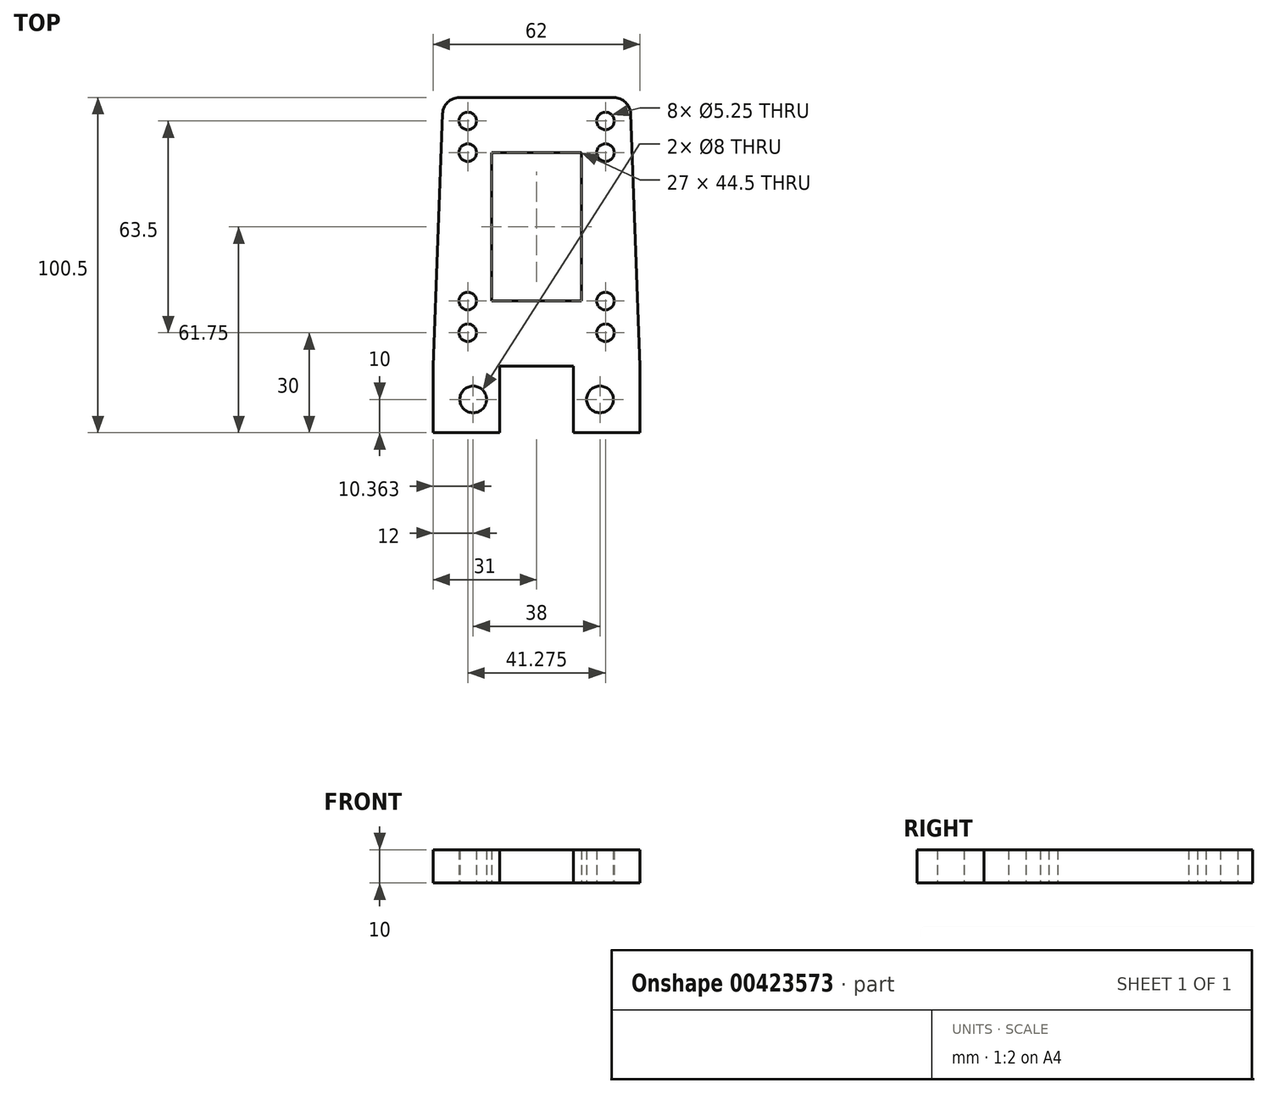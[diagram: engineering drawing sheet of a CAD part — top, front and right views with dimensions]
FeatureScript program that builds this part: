
annotation { "Feature Type Name" : "Feature", "Feature Type Description" : "" }
export const myFeature = defineFeature(function(context is Context, id is Id, definition is map)
    precondition{}
    {
        {
            var Q0;
            Q0=qCreatedBy(makeId("Top.planeOp"),FACE);
            var sketch = newSketch(context, id + "F0", { "sketchPlane" : qUnion([Q0])});
            skLineSegment(sketch, "E0.bottom", {"start": v(28, -50.25) * mm, "end": v(-28, -50.25) * mm});
            skLineSegment(sketch, "E0.top", {"start": v(28, 50.25) * mm, "end": v(-28, 50.25) * mm});
            skLineSegment(sketch, "E0.left", {"start": v(28, -50.25) * mm, "end": v(28, 50.25) * mm});
            skLineSegment(sketch, "E0.right", {"start": v(-28, -50.25) * mm, "end": v(-28, 50.25) * mm});
            skPoint(sketch, "E0.middle", {"position": v(0, 0) * mm});
            skPoint(sketch, "E1", {"position": v(-19, -40.25) * mm});
            skPoint(sketch, "E2", {"position": v(19, -40.25) * mm});
            skLineSegment(sketch, "E3", {"start": v(0, 50.25) * mm, "end": v(0, -50.25) * mm});
            skPoint(sketch, "E4", {"position": v(20.64, -20.25) * mm});
            skPoint(sketch, "E5", {"position": v(-20.64, -20.25) * mm});
            skPoint(sketch, "E6", {"position": v(-20.64, 33.75) * mm});
            skPoint(sketch, "E7", {"position": v(20.64, 33.75) * mm});
            skPoint(sketch, "E8", {"position": v(0, 33.75) * mm});
            skLineSegment(sketch, "E9.bottom", {"start": v(11.05, -50.25) * mm, "end": v(-11.05, -50.25) * mm});
            skLineSegment(sketch, "E9.top", {"start": v(11.05, -30.25) * mm, "end": v(-11.05, -30.25) * mm});
            skLineSegment(sketch, "E9.left", {"start": v(11.05, -50.25) * mm, "end": v(11.05, -30.25) * mm});
            skLineSegment(sketch, "E9.right", {"start": v(-11.05, -50.25) * mm, "end": v(-11.05, -30.25) * mm});
            skPoint(sketch, "E9.middle", {"position": v(0, -40.25) * mm});
            skPoint(sketch, "E10", {"position": v(20.64, 43.25) * mm});
            skPoint(sketch, "E11", {"position": v(-20.64, 43.25) * mm});
            skPoint(sketch, "E12", {"position": v(-20.64, -10.75) * mm});
            skPoint(sketch, "E13", {"position": v(20.64, -10.75) * mm});
            skPoint(sketch, "E14", {"position": v(0, -10.75) * mm});
            skPoint(sketch, "E15", {"position": v(0, 11.5) * mm});
            skLineSegment(sketch, "E16", {"start": v(28, -50.25) * mm, "end": v(31, -50.25) * mm});
            skLineSegment(sketch, "E17", {"start": v(31, -50.25) * mm, "end": v(31, -30.25) * mm});
            skLineSegment(sketch, "E18", {"start": v(31, -30.25) * mm, "end": v(28, 50.25) * mm});
            skLineSegment(sketch, "E19", {"start": v(-28, -50.25) * mm, "end": v(-31, -50.25) * mm});
            skLineSegment(sketch, "E20", {"start": v(-31, -50.25) * mm, "end": v(-31, -30.25) * mm});
            skLineSegment(sketch, "E21", {"start": v(-31, -30.25) * mm, "end": v(-28, 50.25) * mm});
            skLineSegment(sketch, "E22.bottom", {"start": v(13.5, -10.75) * mm, "end": v(-13.5, -10.75) * mm});
            skLineSegment(sketch, "E22.top", {"start": v(13.5, 33.75) * mm, "end": v(-13.5, 33.75) * mm});
            skLineSegment(sketch, "E22.left", {"start": v(13.5, -10.75) * mm, "end": v(13.5, 33.75) * mm});
            skLineSegment(sketch, "E22.right", {"start": v(-13.5, -10.75) * mm, "end": v(-13.5, 33.75) * mm});
            skSolve(sketch);
        }
        {
            var Q0;
            {var subQ0=sQuery(id+"F0.wireOp",EDGE,"E0.right");Q0=makeQuery(id+"F0.imprint","IMPRINT",FACE,{"disambiguationData":[TD([[makeQuery(id+"F0.imprint","IMPRINT",EDGE,{"derivedFrom":subQ0}),-1.0]])]});}
            var Q1;
            {var subQ5=sQuery(id+"F0.wireOp",EDGE,"E0.left");Q1=makeQuery(id+"F0.imprint","IMPRINT",FACE,{"disambiguationData":[TD([[makeQuery(id+"F0.imprint","IMPRINT",EDGE,{"derivedFrom":subQ5}),1.0]])]});}
            var Q2;
            Q2=makeQuery(id+"F0.imprint","IMPRINT",FACE,{"disambiguationData":[TD([[makeQuery(id+"F0.imprint","IMPRINT",EDGE,{"derivedFrom":sQuery(id+"F0.wireOp",EDGE,"E0.right")}),1.0]])]});
            var Q3;
            Q3=makeQuery(id+"F0.imprint","IMPRINT",FACE,{"disambiguationData":[TD([[makeQuery(id+"F0.imprint","IMPRINT",EDGE,{"derivedFrom":sQuery(id+"F0.wireOp",EDGE,"E0.left")}),-1.0]])]});
            extrude(context, id + "F1", {"entities" : qUnion([Q0, Q1, Q2, Q3]), "depth" : 10 * mm});
        }
        {
            var Q0;
            Q0=sQuery(id+"F0.wireOp",VERTEX,"E4");
            var Q1;
            Q1=sQuery(id+"F0.wireOp",VERTEX,"E5");
            var Q2;
            Q2=sQuery(id+"F0.wireOp",VERTEX,"E6");
            var Q3;
            Q3=sQuery(id+"F0.wireOp",VERTEX,"E7");
            var Q4;
            Q4=sQuery(id+"F0.wireOp",VERTEX,"E11");
            var Q5;
            Q5=sQuery(id+"F0.wireOp",VERTEX,"E10");
            var Q6;
            Q6=sQuery(id+"F0.wireOp",VERTEX,"E13");
            var Q7;
            Q7=sQuery(id+"F0.wireOp",VERTEX,"E12");
            var Q8;
            Q8=makeQuery(id+"F1.opExtrude","SWEPT_BODY",BODY,{"disambiguationData":[OSD([sQuery(id+"F0.wireOp",EDGE,"E0.bottom"),sQuery(id+"F0.wireOp",EDGE,"E0.top"),sQuery(id+"F0.wireOp",EDGE,"E0.left"),sQuery(id+"F0.wireOp",EDGE,"E0.right"),sQuery(id+"F0.wireOp",EDGE,"L21EXdMg-1EtD-Z7vm-donr-5LUVcZekd0gJ.bottom"),sQuery(id+"F0.wireOp",EDGE,"L21EXdMg-1EtD-Z7vm-donr-5LUVcZekd0gJ.top"),sQuery(id+"F0.wireOp",EDGE,"L21EXdMg-1EtD-Z7vm-donr-5LUVcZekd0gJ.left"),sQuery(id+"F0.wireOp",EDGE,"L21EXdMg-1EtD-Z7vm-donr-5LUVcZekd0gJ.right")])]});
            hole(context, id + "F2", {"style" : HoleStyle.SIMPLE, "endStyle" : HoleEndStyle.THROUGH, "oppositeDirection" : true, "standardTappedOrClearance" : lookupTablePath({ "standard" : "ISO", "fit" : "Close", "size" : "M5", "type" : "Clearance" }), "standardBlindInLast" : lookupTablePath({ "fit" : "Close", "standard" : "ISO", "size" : "M5", "type" : "Clearance" }), "holeDiameter" : 5.25 * mm, "isTappedThrough" : true, "tappedDepth" : 12 * mm, "tapClearance" : 3, "locations" : qUnion([Q0, Q1, Q2, Q3, Q4, Q5, Q6, Q7]), "scope" : qUnion([Q8])});
        }
        {
            var Q0;
            Q0=sQuery(id+"F0.wireOp",VERTEX,"E1");
            var Q1;
            Q1=sQuery(id+"F0.wireOp",VERTEX,"E2");
            var Q2;
            Q2=makeQuery(id+"F1.opExtrude","SWEPT_BODY",BODY,{"disambiguationData":[OSD([sQuery(id+"F0.wireOp",EDGE,"E0.bottom"),sQuery(id+"F0.wireOp",EDGE,"E0.top"),sQuery(id+"F0.wireOp",EDGE,"E0.left"),sQuery(id+"F0.wireOp",EDGE,"E0.right"),sQuery(id+"F0.wireOp",EDGE,"L21EXdMg-1EtD-Z7vm-donr-5LUVcZekd0gJ.bottom"),sQuery(id+"F0.wireOp",EDGE,"L21EXdMg-1EtD-Z7vm-donr-5LUVcZekd0gJ.top"),sQuery(id+"F0.wireOp",EDGE,"L21EXdMg-1EtD-Z7vm-donr-5LUVcZekd0gJ.left"),sQuery(id+"F0.wireOp",EDGE,"L21EXdMg-1EtD-Z7vm-donr-5LUVcZekd0gJ.right")])]});
            hole(context, id + "F3", {"style" : HoleStyle.SIMPLE, "endStyle" : HoleEndStyle.THROUGH, "oppositeDirection" : true, "standardTappedOrClearance" : lookupTablePath({ "standard" : "ISO", "size" : "8", "type" : "Drilled" }), "standardBlindInLast" : lookupTablePath({ "standard" : "ISO", "size" : "8", "type" : "Drilled" }), "holeDiameter" : 8 * mm, "isTappedThrough" : true, "tappedDepth" : 12 * mm, "tapClearance" : 3, "locations" : qUnion([Q0, Q1]), "scope" : qUnion([Q2])});
        }
        {
            var Q0;
            Q0=makeQuery(id+"F1.opExtrude","SWEPT_EDGE",EDGE,{"disambiguationData":[OSD([sQuery(id+"F0.wireOp",EDGE,"E0.top"),sQuery(id+"F0.wireOp",EDGE,"E0.left")])]});
            var Q1;
            Q1=makeQuery(id+"F1.opExtrude","SWEPT_EDGE",EDGE,{"disambiguationData":[OSD([sQuery(id+"F0.wireOp",EDGE,"E0.top"),sQuery(id+"F0.wireOp",EDGE,"E0.right")])]});
            fillet(context, id + "F4", {"entities" : qUnion([Q0, Q1]), "radius" : 5 * mm, "tangentPropagation" : true, "allowEdgeOverflow" : false});
        }
    });
